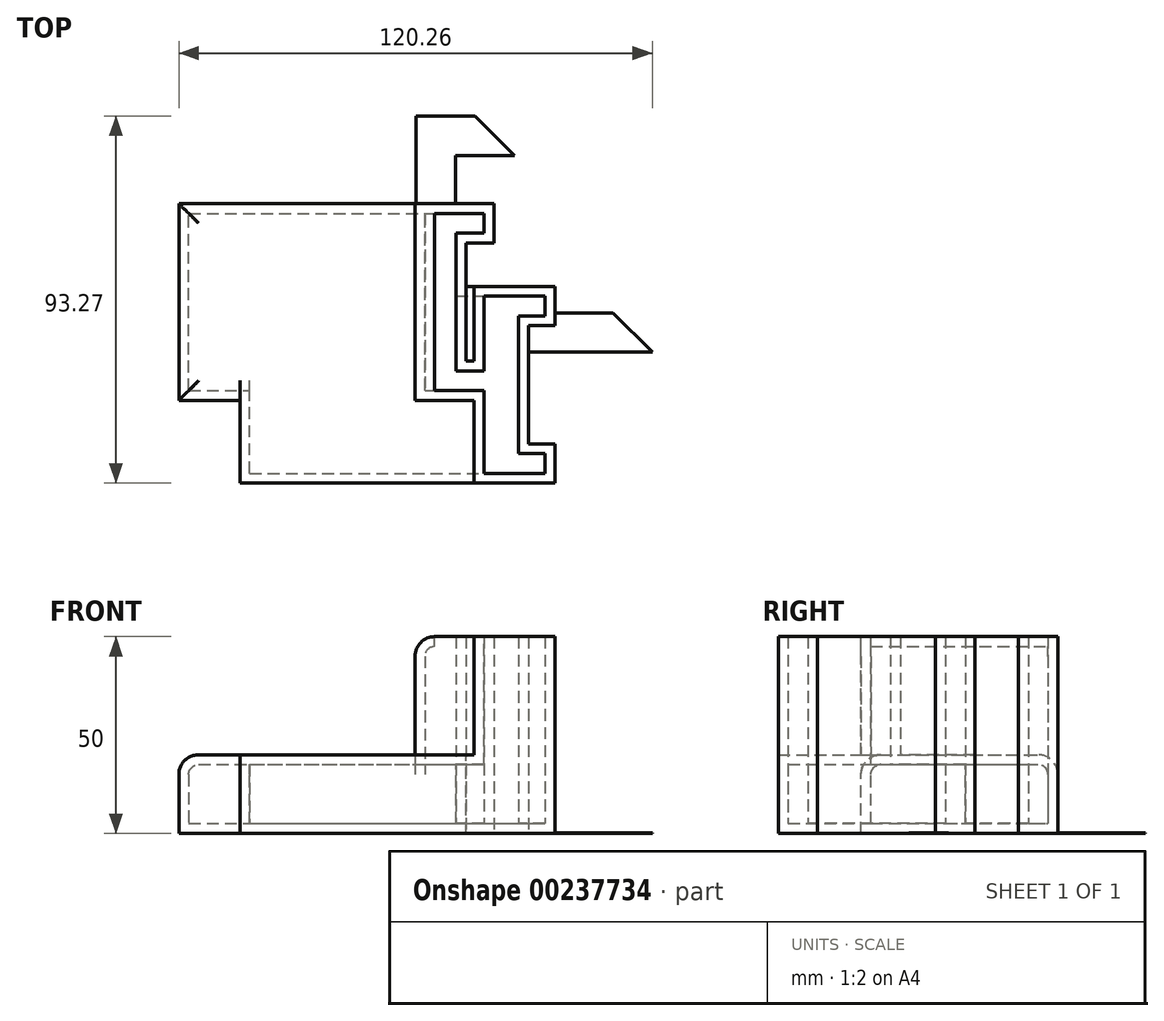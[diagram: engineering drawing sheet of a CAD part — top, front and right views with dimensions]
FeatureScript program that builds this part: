
annotation { "Feature Type Name" : "Feature", "Feature Type Description" : "" }
export const myFeature = defineFeature(function(context is Context, id is Id, definition is map)
    precondition{}
    {
        {
            var Q0;
            Q0=qCreatedBy(makeId("Top.planeOp"),FACE);
            var sketch = newSketch(context, id + "F0", { "sketchPlane" : qUnion([Q0])});
            skLineSegment(sketch, "E0", {"start": v(13.87, 53.27) * mm, "end": v(-1.13, 53.27) * mm});
            skLineSegment(sketch, "E1", {"start": v(-1.13, 53.27) * mm, "end": v(-1.13, -6.73) * mm});
            skLineSegment(sketch, "E2", {"start": v(-1.13, -6.73) * mm, "end": v(58.87, -6.73) * mm});
            skLineSegment(sketch, "E3", {"start": v(58.87, -6.73) * mm, "end": v(48.87, 3.27) * mm});
            skLineSegment(sketch, "E4", {"start": v(48.87, 3.27) * mm, "end": v(8.87, 3.27) * mm});
            skLineSegment(sketch, "E5", {"start": v(8.87, 3.27) * mm, "end": v(8.87, 43.27) * mm});
            skLineSegment(sketch, "E6", {"start": v(8.87, 43.27) * mm, "end": v(23.87, 43.27) * mm});
            skLineSegment(sketch, "E7", {"start": v(23.87, 43.27) * mm, "end": v(13.87, 53.27) * mm});
            skSolve(sketch);
        }
        {
            var Q0;
            Q0 = qSketchRegion(id + "F0", true);
            extrude(context, id + "F1", {"entities" : qUnion([Q0]), "depth" : 0.2 * mm});
        }
        {
            var Q0;
            Q0=qCreatedBy(makeId("Top.planeOp"),FACE);
            var sketch = newSketch(context, id + "F2", { "sketchPlane" : qUnion([Q0])});
            skLineSegment(sketch, "E8.bottom", {"start": v(-61.39, -18.96) * mm, "end": v(-1.39, -18.96) * mm});
            skLineSegment(sketch, "E8.top", {"start": v(-61.39, 31.04) * mm, "end": v(-1.39, 31.04) * mm});
            skLineSegment(sketch, "E8.left", {"start": v(-61.39, -18.96) * mm, "end": v(-61.39, 31.04) * mm});
            skLineSegment(sketch, "E8.right", {"start": v(-1.39, -18.96) * mm, "end": v(-1.39, 31.04) * mm});
            skLineSegment(sketch, "E9.bottom", {"start": v(-1.39, -18.96) * mm, "end": v(18.61, -18.96) * mm});
            skLineSegment(sketch, "E9.top", {"start": v(-1.39, 31.04) * mm, "end": v(18.61, 31.04) * mm});
            skLineSegment(sketch, "E9.right", {"start": v(18.61, -18.96) * mm, "end": v(18.61, 31.04) * mm});
            skLineSegment(sketch, "E10.bottom", {"start": v(18.61, 21.04) * mm, "end": v(11.57, 21.04) * mm});
            skLineSegment(sketch, "E10.top", {"start": v(18.61, -8.96) * mm, "end": v(11.57, -8.96) * mm});
            skLineSegment(sketch, "E10.left", {"start": v(18.61, 21.04) * mm, "end": v(18.61, -8.96) * mm});
            skLineSegment(sketch, "E10.right", {"start": v(11.57, 21.04) * mm, "end": v(11.57, -8.96) * mm});
            skSolve(sketch);
        }
        {
            var Q0;
            Q0=makeQuery(id+"F2.imprint","IMPRINT",FACE,{"disambiguationData":[TD([[makeQuery(id+"F2.imprint","IMPRINT",EDGE,{"derivedFrom":sQuery(id+"F2.wireOp",EDGE,"E8.bottom")}),1.0]])]});
            extrude(context, id + "F3", {"entities" : qUnion([Q0]), "depth" : 20 * mm});
        }
        {
            var Q0;
            {var subQ1=sQuery(id+"F2.wireOp",EDGE,"E9.bottom");Q0=makeQuery(id+"F2.imprint","IMPRINT",FACE,{"disambiguationData":[TD([[makeQuery(id+"F2.imprint","IMPRINT",EDGE,{"derivedFrom":subQ1}),1.0]])]});}
            extrude(context, id + "F4", {"entities" : qUnion([Q0]), "operationType" : NewBodyOperationType.ADD, "depth" : 50 * mm});
        }
        {
            var Q0;
            Q0=qCreatedBy(makeId("Top.planeOp"),FACE);
            var sketch = newSketch(context, id + "F5", { "sketchPlane" : qUnion([Q0])});
            skLineSegment(sketch, "E11.bottom", {"start": v(-45.9, -40) * mm, "end": v(13.57, -40) * mm});
            skLineSegment(sketch, "E11.top", {"start": v(-45.9, 10) * mm, "end": v(13.57, 10) * mm});
            skLineSegment(sketch, "E11.left", {"start": v(-45.9, -40) * mm, "end": v(-45.9, 10) * mm});
            skLineSegment(sketch, "E11.right", {"start": v(13.57, -40) * mm, "end": v(13.57, 10) * mm});
            skLineSegment(sketch, "E12.bottom", {"start": v(13.57, -40) * mm, "end": v(34.1, -40) * mm});
            skLineSegment(sketch, "E12.top", {"start": v(13.57, 10) * mm, "end": v(34.1, 10) * mm});
            skLineSegment(sketch, "E12.right", {"start": v(34.1, -40) * mm, "end": v(34.1, 10) * mm});
            skLineSegment(sketch, "E13.bottom", {"start": v(34.1, 0) * mm, "end": v(27.43, 0) * mm});
            skLineSegment(sketch, "E13.top", {"start": v(34.1, -30) * mm, "end": v(27.43, -30) * mm});
            skLineSegment(sketch, "E13.left", {"start": v(34.1, 0) * mm, "end": v(34.1, -30) * mm});
            skLineSegment(sketch, "E13.right", {"start": v(27.43, 0) * mm, "end": v(27.43, -30) * mm});
            skSolve(sketch);
        }
        {
            var Q0;
            Q0=makeQuery(id+"F5.imprint","IMPRINT",FACE,{"disambiguationData":[TD([[makeQuery(id+"F5.imprint","IMPRINT",EDGE,{"derivedFrom":sQuery(id+"F5.wireOp",EDGE,"E11.bottom")}),1.0]])]});
            extrude(context, id + "F6", {"entities" : qUnion([Q0]), "depth" : 20 * mm});
        }
        {
            var Q0;
            {var subQ1=sQuery(id+"F5.wireOp",EDGE,"E12.bottom");Q0=makeQuery(id+"F5.imprint","IMPRINT",FACE,{"disambiguationData":[TD([[makeQuery(id+"F5.imprint","IMPRINT",EDGE,{"derivedFrom":subQ1}),1.0]])]});}
            extrude(context, id + "F7", {"entities" : qUnion([Q0]), "operationType" : NewBodyOperationType.ADD, "depth" : 50 * mm});
        }
        {
            var Q0;
            Q0=makeQuery(id+"F4.opExtrude","CAP_EDGE",EDGE,{"disambiguationData":[OSD([sQuery(id+"F2.wireOp",EDGE,"E8.right")])],"isStart":false});
            var Q1;
            Q1=makeQuery(id+"F3.opExtrude","CAP_EDGE",EDGE,{"disambiguationData":[OSD([sQuery(id+"F2.wireOp",EDGE,"E8.left")])],"isStart":false});
            var Q2;
            Q2=makeQuery(id+"F3.opExtrude","CAP_EDGE",EDGE,{"disambiguationData":[OSD([sQuery(id+"F2.wireOp",EDGE,"E8.bottom")])],"isStart":false});
            var Q3;
            Q3=makeQuery(id+"F3.opExtrude","CAP_EDGE",EDGE,{"disambiguationData":[OSD([sQuery(id+"F2.wireOp",EDGE,"E8.top")])],"isStart":false});
            fillet(context, id + "F8", {"entities" : qUnion([Q0, Q1, Q2, Q3]), "radius" : 5 * mm, "tangentPropagation" : true, "allowEdgeOverflow" : false});
        }
        {
            var Q0;
            Q0=makeQuery(id+"F4.opExtrude","CAP_FACE",FACE,{"disambiguationData":[OSD([sQuery(id+"F2.wireOp",EDGE,"E9.bottom"),sQuery(id+"F2.wireOp",EDGE,"E9.top"),sQuery(id+"F2.wireOp",EDGE,"E8.right"),sQuery(id+"F2.wireOp",EDGE,"E9.right"),sQuery(id+"F2.wireOp",EDGE,"E10.bottom"),sQuery(id+"F2.wireOp",EDGE,"E10.top"),sQuery(id+"F2.wireOp",EDGE,"E10.right")])],"isStart":false});
            shell(context, id + "F9", {"entities" : qUnion([Q0]), "thickness" : 2.5 * mm});
        }
    });
